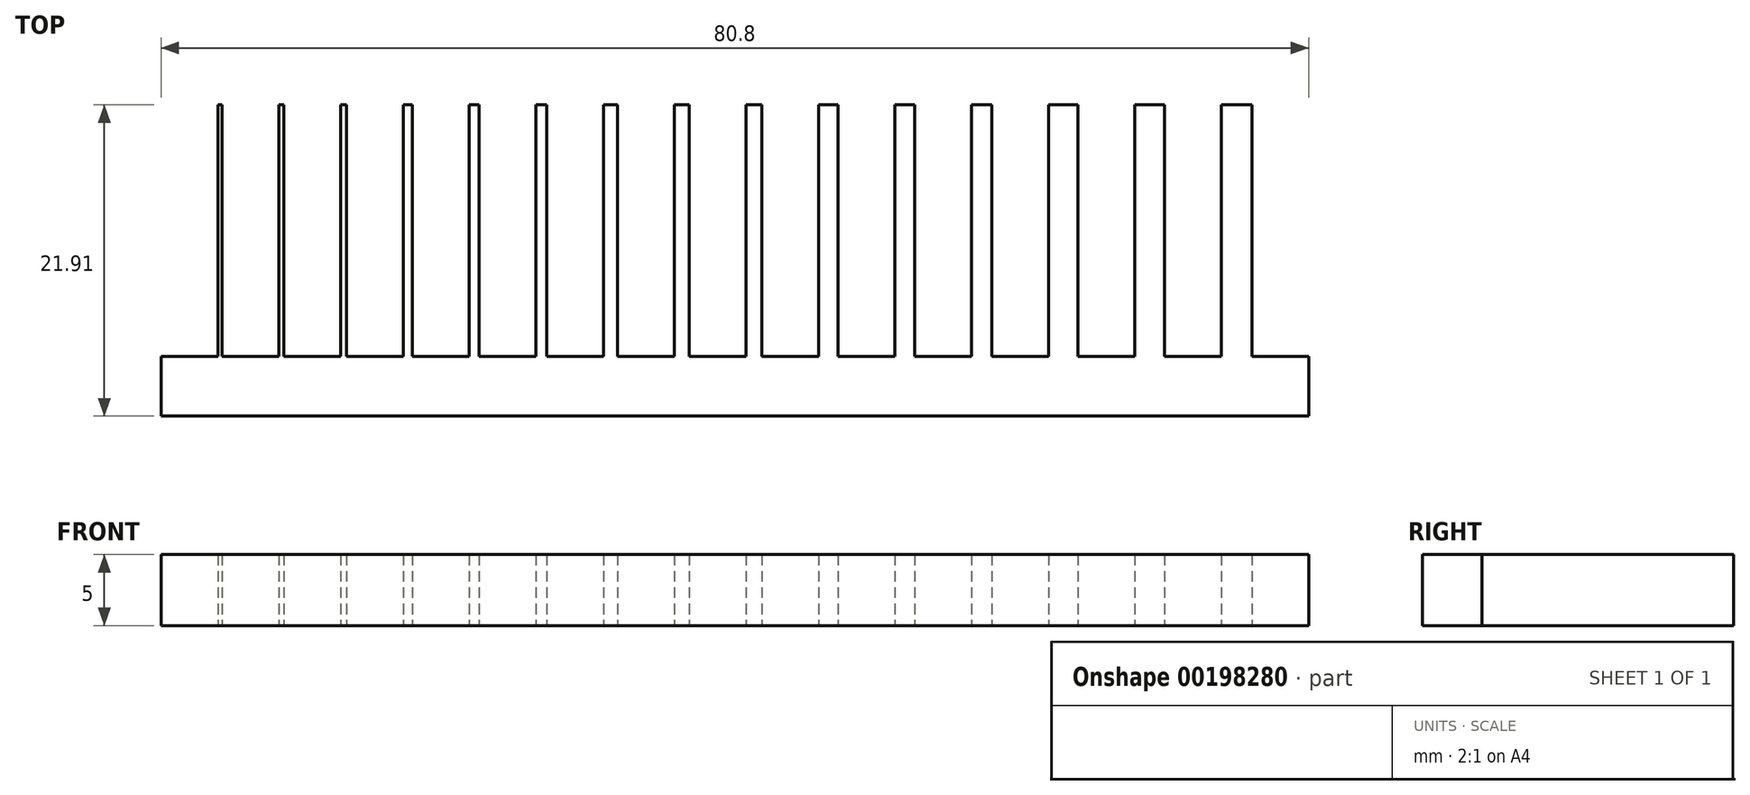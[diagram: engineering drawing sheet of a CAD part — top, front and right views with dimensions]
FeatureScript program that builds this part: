
annotation { "Feature Type Name" : "Feature", "Feature Type Description" : "" }
export const myFeature = defineFeature(function(context is Context, id is Id, definition is map)
    precondition{}
    {
        {
            var Q0;
            Q0=qCreatedBy(makeId("Top.planeOp"),FACE);
            var sketch = newSketch(context, id + "F0", { "sketchPlane" : qUnion([Q0])});
            skLineSegment(sketch, "E0", {"start": v(0, 0) * mm, "end": v(0, 4.2) * mm});
            skLineSegment(sketch, "E1", {"start": v(0, 4.2) * mm, "end": v(4, 4.2) * mm});
            skLineSegment(sketch, "E2", {"start": v(4, 4.2) * mm, "end": v(4, 21.91) * mm});
            skLineSegment(sketch, "E3", {"start": v(4, 21.91) * mm, "end": v(4.3, 21.91) * mm});
            skLineSegment(sketch, "E4", {"start": v(4.3, 21.91) * mm, "end": v(4.3, 4.2) * mm});
            skLineSegment(sketch, "E5", {"start": v(4.3, 4.2) * mm, "end": v(8.3, 4.2) * mm});
            skLineSegment(sketch, "E6", {"start": v(8.3, 4.2) * mm, "end": v(8.3, 21.91) * mm});
            skLineSegment(sketch, "E7", {"start": v(8.3, 21.91) * mm, "end": v(8.65, 21.91) * mm});
            skLineSegment(sketch, "E8", {"start": v(8.65, 21.91) * mm, "end": v(8.65, 4.2) * mm});
            skLineSegment(sketch, "E9", {"start": v(8.65, 4.2) * mm, "end": v(12.65, 4.2) * mm});
            skLineSegment(sketch, "E10", {"start": v(12.65, 4.2) * mm, "end": v(12.65, 21.91) * mm});
            skLineSegment(sketch, "E11", {"start": v(12.65, 21.91) * mm, "end": v(13.05, 21.91) * mm});
            skLineSegment(sketch, "E12", {"start": v(13.05, 21.91) * mm, "end": v(13.05, 4.2) * mm});
            skLineSegment(sketch, "E13", {"start": v(13.05, 4.2) * mm, "end": v(17.05, 4.2) * mm});
            skLineSegment(sketch, "E14", {"start": v(17.05, 4.2) * mm, "end": v(17.05, 21.91) * mm});
            skLineSegment(sketch, "E15", {"start": v(17.05, 21.91) * mm, "end": v(17.7, 21.91) * mm});
            skLineSegment(sketch, "E16", {"start": v(17.7, 21.91) * mm, "end": v(17.7, 4.2) * mm});
            skLineSegment(sketch, "E17", {"start": v(17.7, 4.2) * mm, "end": v(21.7, 4.2) * mm});
            skLineSegment(sketch, "E18", {"start": v(21.7, 4.2) * mm, "end": v(21.7, 21.91) * mm});
            skLineSegment(sketch, "E19", {"start": v(21.7, 21.91) * mm, "end": v(22.4, 21.91) * mm});
            skLineSegment(sketch, "E20", {"start": v(22.4, 21.91) * mm, "end": v(22.4, 4.2) * mm});
            skLineSegment(sketch, "E21", {"start": v(22.4, 4.2) * mm, "end": v(26.4, 4.2) * mm});
            skLineSegment(sketch, "E22", {"start": v(26.4, 4.2) * mm, "end": v(26.4, 21.91) * mm});
            skLineSegment(sketch, "E23", {"start": v(26.4, 21.91) * mm, "end": v(27.15, 21.91) * mm});
            skLineSegment(sketch, "E24", {"start": v(27.15, 21.91) * mm, "end": v(27.15, 4.2) * mm});
            skLineSegment(sketch, "E25", {"start": v(27.15, 4.2) * mm, "end": v(31.15, 4.2) * mm});
            skLineSegment(sketch, "E26", {"start": v(31.15, 4.2) * mm, "end": v(31.15, 21.91) * mm});
            skLineSegment(sketch, "E27", {"start": v(31.15, 21.91) * mm, "end": v(32.15, 21.91) * mm});
            skLineSegment(sketch, "E28", {"start": v(32.15, 21.91) * mm, "end": v(32.15, 4.2) * mm});
            skLineSegment(sketch, "E29", {"start": v(32.15, 4.2) * mm, "end": v(36.15, 4.2) * mm});
            skLineSegment(sketch, "E30", {"start": v(36.15, 4.2) * mm, "end": v(36.15, 21.91) * mm});
            skLineSegment(sketch, "E31", {"start": v(36.15, 21.91) * mm, "end": v(37.2, 21.91) * mm});
            skLineSegment(sketch, "E32", {"start": v(37.2, 21.91) * mm, "end": v(37.2, 4.2) * mm});
            skLineSegment(sketch, "E33", {"start": v(37.2, 4.2) * mm, "end": v(41.2, 4.2) * mm});
            skLineSegment(sketch, "E34", {"start": v(41.2, 4.2) * mm, "end": v(41.2, 21.91) * mm});
            skLineSegment(sketch, "E35", {"start": v(41.2, 21.91) * mm, "end": v(42.3, 21.91) * mm});
            skLineSegment(sketch, "E36", {"start": v(42.3, 21.91) * mm, "end": v(42.3, 4.2) * mm});
            skLineSegment(sketch, "E37", {"start": v(42.3, 4.2) * mm, "end": v(46.3, 4.2) * mm});
            skLineSegment(sketch, "E38", {"start": v(46.3, 4.2) * mm, "end": v(46.3, 21.91) * mm});
            skLineSegment(sketch, "E39", {"start": v(46.3, 21.91) * mm, "end": v(47.65, 21.91) * mm});
            skLineSegment(sketch, "E40", {"start": v(47.65, 21.91) * mm, "end": v(47.65, 4.2) * mm});
            skLineSegment(sketch, "E41", {"start": v(47.65, 4.2) * mm, "end": v(51.65, 4.2) * mm});
            skLineSegment(sketch, "E42", {"start": v(51.65, 4.2) * mm, "end": v(51.65, 21.91) * mm});
            skLineSegment(sketch, "E43", {"start": v(51.65, 21.91) * mm, "end": v(53.05, 21.91) * mm});
            skLineSegment(sketch, "E44", {"start": v(53.05, 21.91) * mm, "end": v(53.05, 4.2) * mm});
            skLineSegment(sketch, "E45", {"start": v(53.05, 4.2) * mm, "end": v(57.05, 4.2) * mm});
            skLineSegment(sketch, "E46", {"start": v(57.05, 4.2) * mm, "end": v(57.05, 21.91) * mm});
            skLineSegment(sketch, "E47", {"start": v(57.05, 21.91) * mm, "end": v(58.5, 21.91) * mm});
            skLineSegment(sketch, "E48", {"start": v(58.5, 21.91) * mm, "end": v(58.5, 4.2) * mm});
            skLineSegment(sketch, "E49", {"start": v(58.5, 4.2) * mm, "end": v(62.5, 4.2) * mm});
            skLineSegment(sketch, "E50", {"start": v(62.5, 4.2) * mm, "end": v(62.5, 21.91) * mm});
            skLineSegment(sketch, "E51", {"start": v(62.5, 21.91) * mm, "end": v(64.55, 21.91) * mm});
            skLineSegment(sketch, "E52", {"start": v(64.55, 21.91) * mm, "end": v(64.55, 4.2) * mm});
            skLineSegment(sketch, "E53", {"start": v(64.55, 4.2) * mm, "end": v(68.55, 4.2) * mm});
            skLineSegment(sketch, "E54", {"start": v(68.55, 4.2) * mm, "end": v(68.55, 21.91) * mm});
            skLineSegment(sketch, "E55", {"start": v(68.55, 21.91) * mm, "end": v(70.65, 21.91) * mm});
            skLineSegment(sketch, "E56", {"start": v(70.65, 21.91) * mm, "end": v(70.65, 4.2) * mm});
            skLineSegment(sketch, "E57", {"start": v(70.65, 4.2) * mm, "end": v(74.65, 4.2) * mm});
            skLineSegment(sketch, "E58", {"start": v(74.65, 4.2) * mm, "end": v(74.65, 21.91) * mm});
            skLineSegment(sketch, "E59", {"start": v(74.65, 21.91) * mm, "end": v(76.8, 21.91) * mm});
            skLineSegment(sketch, "E60", {"start": v(76.8, 21.91) * mm, "end": v(76.8, 4.2) * mm});
            skLineSegment(sketch, "E61", {"start": v(76.8, 4.2) * mm, "end": v(80.8, 4.2) * mm});
            skLineSegment(sketch, "E62", {"start": v(80.8, 4.2) * mm, "end": v(80.8, 0) * mm});
            skLineSegment(sketch, "E63", {"start": v(80.8, 0) * mm, "end": v(0, 0) * mm});
            skSolve(sketch);
        }
        {
            var Q0;
            Q0 = qSketchRegion(id + "F0", true);
            extrude(context, id + "F1", {"entities" : qUnion([Q0]), "depth" : 5 * mm});
        }
    });
